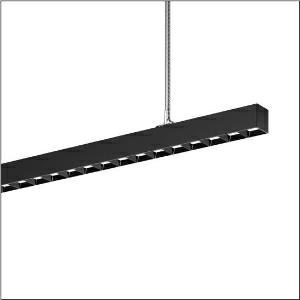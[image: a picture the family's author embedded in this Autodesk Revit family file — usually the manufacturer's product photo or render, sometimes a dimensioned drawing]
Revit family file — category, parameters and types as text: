
# Revit family: silica_r__21_51mx32tctdb_2a66
name_source: partatom
category: Lighting Fixtures
units: mm (PartAtom-declared; Revit-internal decimal feet)

## family parameters
Cut with Voids When Loaded = No
Host = Face
Light Source = No
Part Type = Normal
Room Calculation Point = No
Round Connector Dimension = Use Diameter
Shared = No

## types (1)
- --- (1 x LED, 15540 lm, 133.6 W, 6500K)
    Apparent Load = 134 VA
    CIE Flux Codes = 84 99 100 60 100
    Color Rendering = 80
    Color Temperature = 6500K
    Default Elevation = 1800 mm
    Description = Silica® 21, office luminaire, primary light control with darklight reflector, of PMMA, black, CAT 2 (L<= 3000cd/m²), light emission: direct/indirect distribution, primary light characteristic: symmetric, installation type: suspended mounting, LED, rated luminous flux: 15.540lm, luminous efficacy: 111lm/W, light colour: 8tw, colour temperature: 2700..6500K, control gear: ECG DALI, with terminal, 3+2-pole, max. 2.5mm², mains connection: 220..240V, AC, 50/60Hz, rated input power: 140.3W, luminaire housing, of aluminium, jet black (RAL 9005), length: 3.004mm, width: 53mm, height: 53mm, protection rating (complete): IP20, insulation class (complete): insulation class I (protective earthing), certification: CE, permissible operating ambient temperature: 0..+35°C, standard: EN 50419, packaging unit: 1 piece
    Height = 53 mm
    Lamp = 1 x LED
    Lamp Light Flux = 15540 lm
    Lamp Power = 133.6 W
    Lamp count = 1
    Length = 3004 mm
    Luminous efficacy = 116 lm/W
    Manufacturer = Siteco
    ModVariant = No
    Model = 51MX32TCTDB
    Mounting Place = Ceiling
    Mounting Type = Pendant
    Number of Poles = 1
    OnlyDefault = Yes
    Power Factor = 1
    Product Name = Silica® 21
    Product group = office luminaire | ceiling pendant
    ProductGroupID = 902
    Protection Class = Protection class I
    Protection Degree = IP 20
    RLX_Detail_Level = 1
    RLX_Emergency_Light_Flux = 0 lm
    RLX_Emergency_Type = 0
    RLX_Emergency_Type_DB = No
    RlxData = <blob elided: 63085 chars, md5=51f4a441>
    Socket = socket
    Standby Power = 0 W
    System Light Flux = 15540 lm
    System Power = 134 W
    Type Comments = individual setting
    Type Image = l_1335852.jpg
    URL = http://relux.com
    VarID = @adj_109735
    Voltage = 0 V
    Weight = 0.00 kg
    Width = 53 mm

## geometry (parser evidence)
native form markers: Blend x4, Sweep x11
no freeform markers — native parametric forms only
